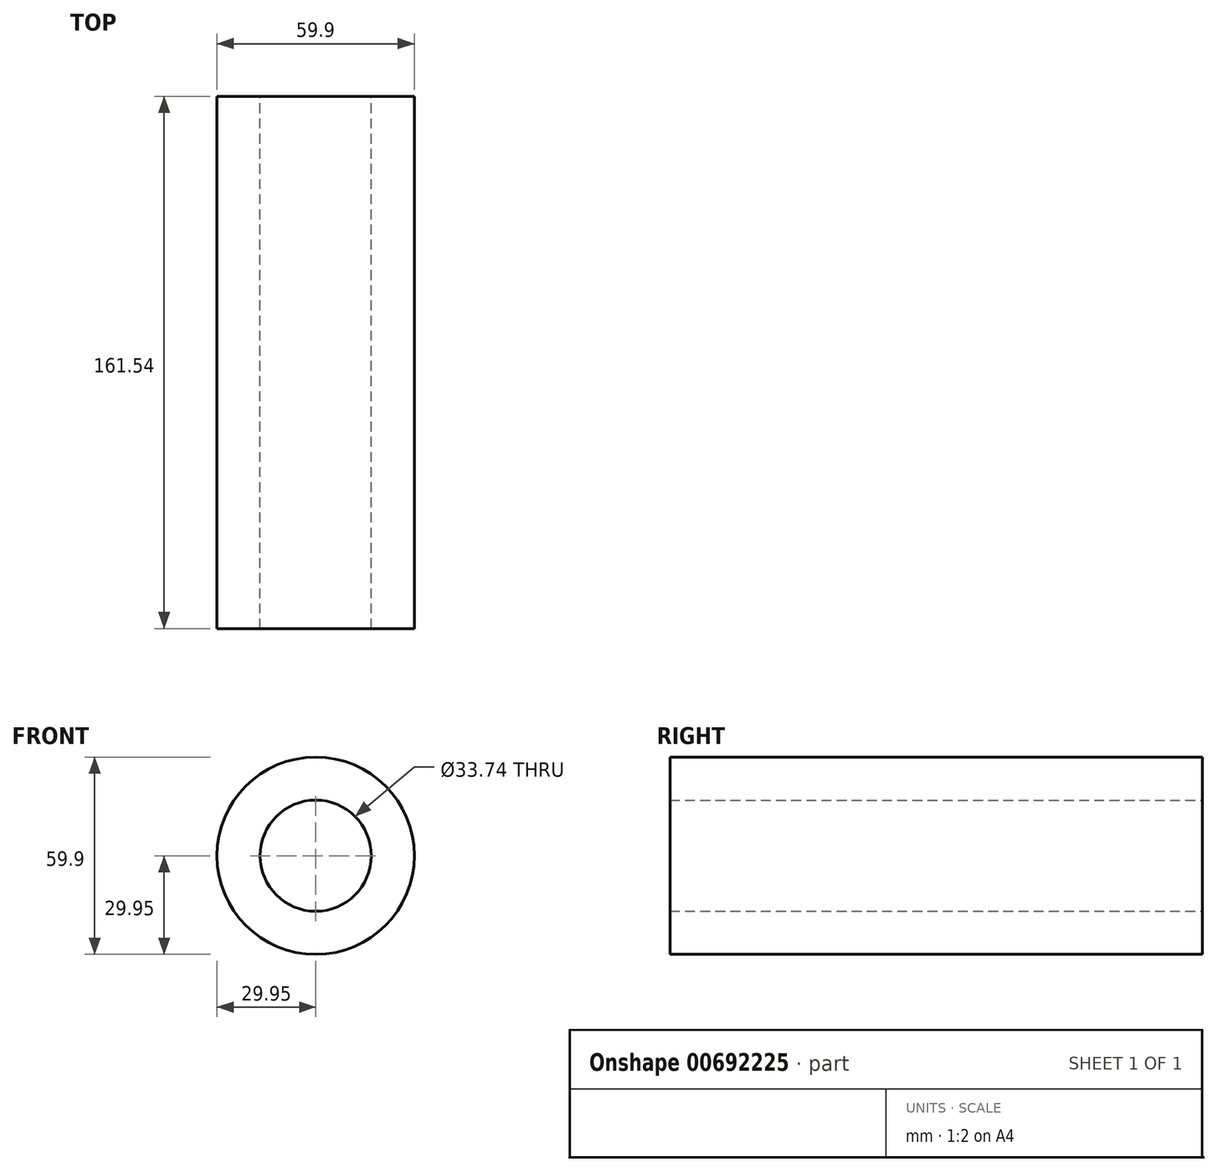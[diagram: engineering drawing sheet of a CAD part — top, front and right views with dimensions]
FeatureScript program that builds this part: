
annotation { "Feature Type Name" : "Feature", "Feature Type Description" : "" }
export const myFeature = defineFeature(function(context is Context, id is Id, definition is map)
    precondition{}
    {
        {
            var Q0;
            Q0=qCreatedBy(makeId("Front.planeOp"),FACE);
            var sketch = newSketch(context, id + "F0", { "sketchPlane" : qUnion([Q0])});
            skCircle(sketch, "E0", {"center": v(0, 0) * mm, "radius": 29.95 * mm});
            skCircle(sketch, "E1", {"center": v(0, 0) * mm, "radius": 16.87 * mm});
            skSolve(sketch);
        }
        {
            var Q0;
            Q0 = qSketchRegion(id + "F0", true);
            extrude(context, id + "F1", {"entities" : qUnion([Q0]), "endBound" : BoundingType.SYMMETRIC, "depth" : 161.54 * mm, "offsetDistance" : 25.4 * mm});
        }
    });
